# Revit family: LP_Балансировочный_клапан_Auto_РОСТерм_v.1.0
name_source: partatom
category: Арматура трубопроводов
units: mm (PartAtom-declared; Revit-internal decimal feet)

## family parameters
Всегда вертикально = Нет
На основе рабочей плоскости = Нет
Общий = Нет
При загрузке вырезать с полостями = Нет
Размер круглого соединителя = Использовать диаметр
Тип детали = Нормальный

## types (1)
- HEIZEN AUTO
    ADSK_Версия Revit = 2017
    ADSK_Единица измерения = шт.
    ADSK_Завод-изготовитель = Heizen
    ADSK_Количество = 1
    DN15 = BIMLIB_Балансировочный_клапан_Auto_РОСТерм_DN15 : DN15
    DN20 = BIMLIB_Балансировочный_клапан_Auto_РОСТерм_DN20 : DN20
    DN25 = BIMLIB_Балансировочный_клапан_Auto_РОСТерм_DN25 : DN25
    DN32 = BIMLIB_Балансировочный_клапан_Auto_РОСТерм_DN32 : DN32
    DN40 = BIMLIB_Балансировочный_клапан_Auto_РОСТерм_DN40 : DN40
    DN50 = BIMLIB_Балансировочный_клапан_Auto_РОСТерм_DN50 : DN50
    Изготовитель = РОСТерм
    Коэффициент K = 0
    Отметка по умолчанию = 0 мм
    РТ_Материал_КорпусКлапана = РОСТ_Латунь
    РТ_Материал_ЭлементРукоятки = Heizen_Пластик_черный
    РТ_Материал_ЭлементыКорпуса = Heizen_Пластик_красный
    РТ_Номинальное давление = 25.0 бары
